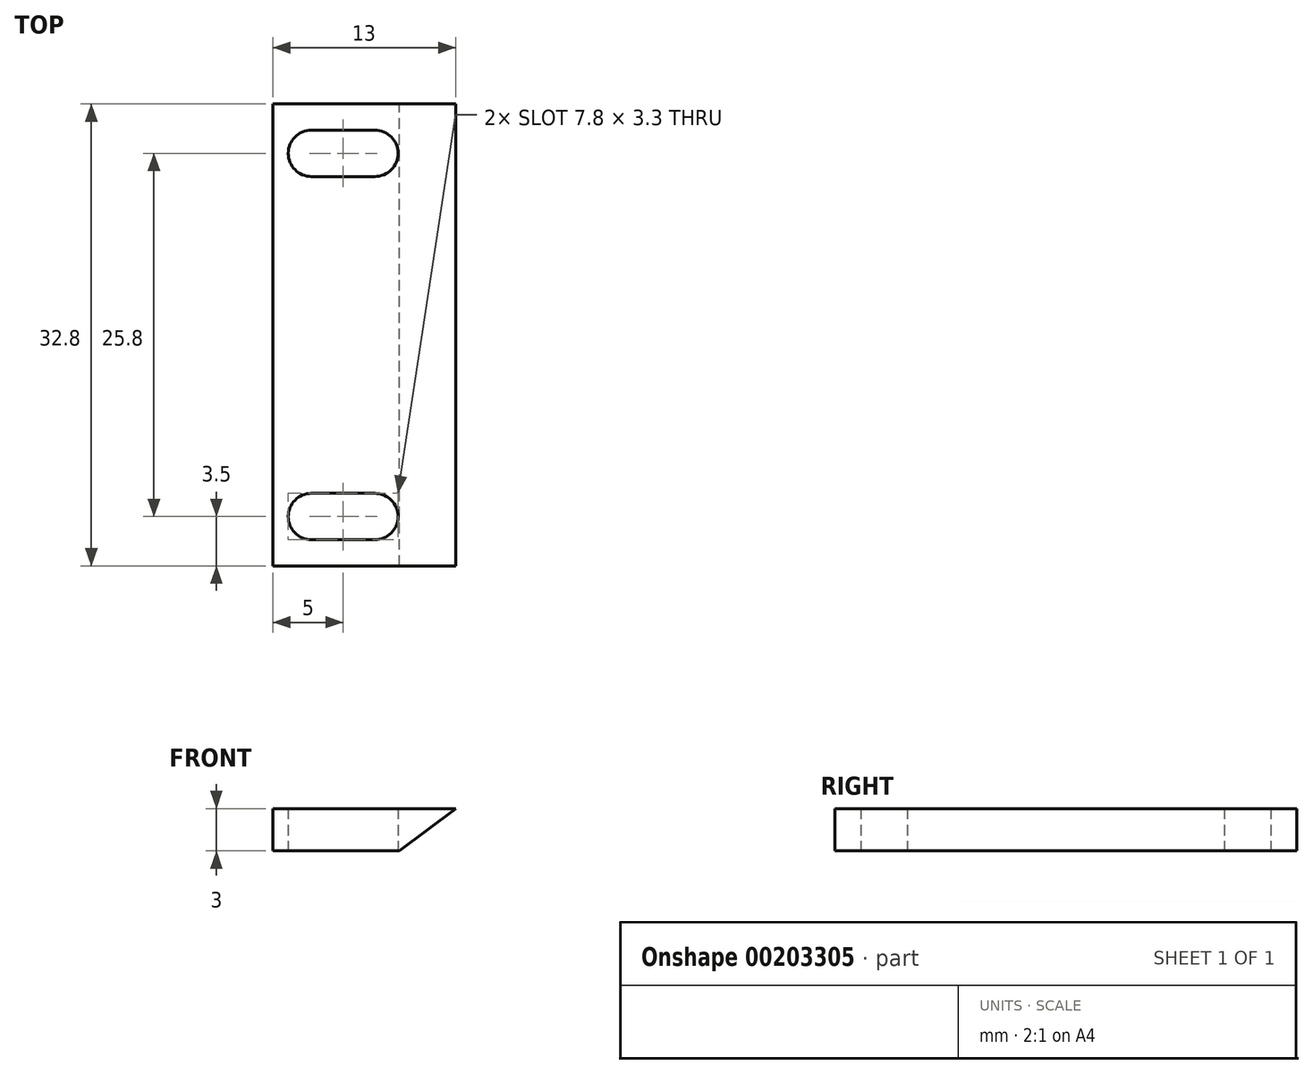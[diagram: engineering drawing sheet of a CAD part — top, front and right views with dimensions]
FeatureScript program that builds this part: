
annotation { "Feature Type Name" : "Feature", "Feature Type Description" : "" }
export const myFeature = defineFeature(function(context is Context, id is Id, definition is map)
    precondition{}
    {
        {
            var Q0;
            Q0=qCreatedBy(makeId("Top.planeOp"),FACE);
            var sketch = newSketch(context, id + "F0", { "sketchPlane" : qUnion([Q0])});
            skLineSegment(sketch, "E0.bottom", {"start": v(-5, 16.4) * mm, "end": v(8, 16.4) * mm});
            skLineSegment(sketch, "E0.top", {"start": v(-5, -16.4) * mm, "end": v(8, -16.4) * mm});
            skLineSegment(sketch, "E0.left", {"start": v(-5, 16.4) * mm, "end": v(-5, -16.4) * mm});
            skLineSegment(sketch, "E0.right", {"start": v(8, 16.4) * mm, "end": v(8, -16.4) * mm});
            skLineSegment(sketch, "E1", {"start": v(-12.07, 12.9) * mm, "end": v(15.8, 12.9) * mm, "construction": true});
            skLineSegment(sketch, "E2", {"start": v(-12.07, -12.9) * mm, "end": v(16.66, -12.9) * mm, "construction": true});
            skArc(sketch, "E3", {"start": v(-2.25, 14.55) * mm, "mid": v(-3.9, 12.9) * mm, "end": v(-2.25, 11.25) * mm});
            skArc(sketch, "E4", {"start": v(2.25, 11.25) * mm, "mid": v(3.9, 12.9) * mm, "end": v(2.25, 14.55) * mm});
            skLineSegment(sketch, "E5", {"start": v(-2.25, 14.55) * mm, "end": v(2.25, 14.55) * mm});
            skLineSegment(sketch, "E6", {"start": v(-2.25, 11.25) * mm, "end": v(2.25, 11.25) * mm});
            skArc(sketch, "E7.MirrorCS", {"start": v(-2.25, -14.55) * mm, "mid": v(-3.9, -12.9) * mm, "end": v(-2.25, -11.25) * mm});
            skLineSegment(sketch, "E8.MirrorCS", {"start": v(-2.25, -14.55) * mm, "end": v(2.25, -14.55) * mm});
            skArc(sketch, "E9.MirrorCS", {"start": v(2.25, -11.25) * mm, "mid": v(3.9, -12.9) * mm, "end": v(2.25, -14.55) * mm});
            skLineSegment(sketch, "E10.MirrorCS", {"start": v(-2.25, -11.25) * mm, "end": v(2.25, -11.25) * mm});
            skSolve(sketch);
        }
        {
            var Q0;
            Q0 = qSketchRegion(id + "F0", true);
            extrude(context, id + "F1", {"entities" : qUnion([Q0]), "depth" : 3 * mm});
        }
        {
            var Q0;
            Q0=makeQuery(id+"F1.opExtrude","SWEPT_FACE",FACE,{"disambiguationData":[OSD([sQuery(id+"F0.wireOp",EDGE,"E0.bottom")])]});
            var sketch = newSketch(context, id + "F2", { "sketchPlane" : qUnion([Q0])});
            skLineSegment(sketch, "E11", {"start": v(-8, 3) * mm, "end": v(-4, 0) * mm});
            skLineSegment(sketch, "E12", {"start": v(-4, 0) * mm, "end": v(-8, 0) * mm});
            skLineSegment(sketch, "E13", {"start": v(-8, 0) * mm, "end": v(-8, 3) * mm});
            skSolve(sketch);
        }
        {
            var Q0;
            Q0 = qSketchRegion(id + "F2", true);
            extrude(context, id + "F3", {"entities" : qUnion([Q0]), "operationType" : NewBodyOperationType.REMOVE, "endBound" : BoundingType.THROUGH_ALL, "oppositeDirection" : true, "depth" : 25 * mm});
        }
    });
